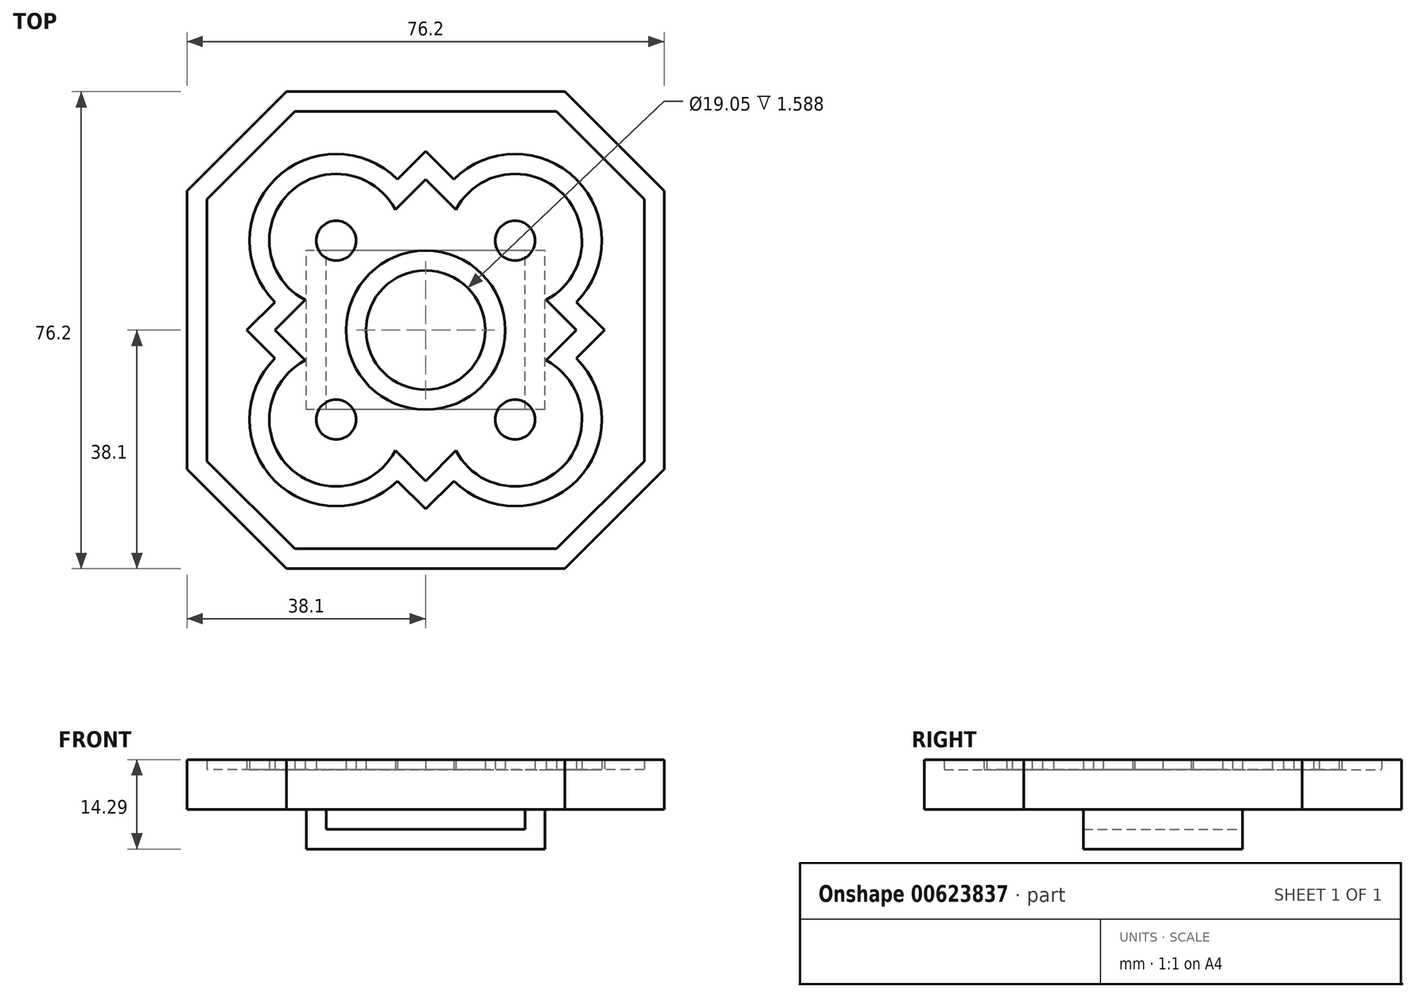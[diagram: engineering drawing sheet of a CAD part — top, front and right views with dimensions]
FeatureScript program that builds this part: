
annotation { "Feature Type Name" : "Feature", "Feature Type Description" : "" }
export const myFeature = defineFeature(function(context is Context, id is Id, definition is map)
    precondition{}
    {
        {
            var Q0;
            Q0=qCreatedBy(makeId("Top.planeOp"),FACE);
            var sketch = newSketch(context, id + "F0", { "sketchPlane" : qUnion([Q0])});
            skLineSegment(sketch, "E0.bottom", {"start": v(-76.2, 0) * mm, "end": v(0, 0) * mm, "construction": true});
            skLineSegment(sketch, "E0.top", {"start": v(-76.2, -76.2) * mm, "end": v(0, -76.2) * mm, "construction": true});
            skLineSegment(sketch, "E0.left", {"start": v(-76.2, 0) * mm, "end": v(-76.2, -76.2) * mm, "construction": true});
            skLineSegment(sketch, "E0.right", {"start": v(0, 0) * mm, "end": v(0, -76.2) * mm, "construction": true});
            skLineSegment(sketch, "E1", {"start": v(-60.32, 0) * mm, "end": v(-15.87, 0) * mm});
            skLineSegment(sketch, "E2", {"start": v(0, -15.87) * mm, "end": v(0, -60.32) * mm});
            skLineSegment(sketch, "E3", {"start": v(-76.2, -15.87) * mm, "end": v(-76.2, -60.32) * mm});
            skLineSegment(sketch, "E4", {"start": v(-60.32, -76.2) * mm, "end": v(-15.87, -76.2) * mm});
            skPoint(sketch, "E5", {"position": v(-38.1, 0) * mm});
            skPoint(sketch, "E6", {"position": v(-76.2, -38.1) * mm});
            skPoint(sketch, "E7", {"position": v(-38.1, -76.2) * mm});
            skPoint(sketch, "E8", {"position": v(0, -38.1) * mm});
            skLineSegment(sketch, "E9", {"start": v(-60.32, -76.2) * mm, "end": v(-76.2, -60.32) * mm});
            skLineSegment(sketch, "E10", {"start": v(0, -60.32) * mm, "end": v(-15.87, -76.2) * mm});
            skLineSegment(sketch, "E11", {"start": v(-76.2, -15.87) * mm, "end": v(-60.32, 0) * mm});
            skLineSegment(sketch, "E12", {"start": v(-15.87, 0) * mm, "end": v(0, -15.87) * mm});
            skLineSegment(sketch, "E13", {"start": v(-38.1, 0) * mm, "end": v(-38.1, -76.2) * mm, "construction": true});
            skPoint(sketch, "E14", {"position": v(-38.1, -38.1) * mm});
            skSolve(sketch);
        }
        {
            var Q0;
            Q0=qSketchRegion(id+"F0",true);
            extrude(context, id + "F1", {"entities" : qUnion([Q0]), "depth" : 6.35 * mm, "offsetDistance" : 25.4 * mm});
        }
        {
            var Q0;
            Q0=makeQuery(id+"F1.opExtrude","CAP_FACE",FACE,{"disambiguationData":[OSD([sQuery(id+"F0.wireOp",EDGE,"E1"),sQuery(id+"F0.wireOp",EDGE,"E2"),sQuery(id+"F0.wireOp",EDGE,"E3"),sQuery(id+"F0.wireOp",EDGE,"E4"),sQuery(id+"F0.wireOp",EDGE,"E9"),sQuery(id+"F0.wireOp",EDGE,"E10"),sQuery(id+"F0.wireOp",EDGE,"E11"),sQuery(id+"F0.wireOp",EDGE,"E12")])],"isStart":false});
            var sketch = newSketch(context, id + "F2", { "sketchPlane" : qUnion([Q0])});
            skLineSegment(sketch, "E15", {"start": v(0, -38.1) * mm, "end": v(-76.2, -38.1) * mm, "construction": true});
            skCircle(sketch, "E16", {"center": v(-38.1, -38.1) * mm, "radius": 12.7 * mm});
            skCircle(sketch, "E17", {"center": v(-38.1, -38.1) * mm, "radius": 9.53 * mm});
            skLineSegment(sketch, "E18", {"start": v(-15.87, 0) * mm, "end": v(-60.32, 0) * mm});
            skLineSegment(sketch, "E19", {"start": v(0, -60.32) * mm, "end": v(-15.88, -76.2) * mm});
            skLineSegment(sketch, "E20", {"start": v(0, -60.32) * mm, "end": v(0, -15.87) * mm});
            skLineSegment(sketch, "E21", {"start": v(0, -15.88) * mm, "end": v(-15.87, 0) * mm});
            skLineSegment(sketch, "E22", {"start": v(-76.2, -15.87) * mm, "end": v(-60.32, 0) * mm});
            skLineSegment(sketch, "E23", {"start": v(-76.2, -60.32) * mm, "end": v(-60.33, -76.2) * mm});
            skLineSegment(sketch, "E24", {"start": v(-76.2, -15.87) * mm, "end": v(-76.2, -60.32) * mm});
            skLineSegment(sketch, "E25", {"start": v(-15.87, -76.2) * mm, "end": v(-60.32, -76.2) * mm});
            skLineSegment(sketch, "E26", {"start": v(-3.18, -59) * mm, "end": v(-3.18, -17.2) * mm});
            skLineSegment(sketch, "E27", {"start": v(-73.03, -59) * mm, "end": v(-73.03, -17.2) * mm});
            skLineSegment(sketch, "E28", {"start": v(-59, -73.02) * mm, "end": v(-17.2, -73.02) * mm});
            skLineSegment(sketch, "E29", {"start": v(-59, -3.17) * mm, "end": v(-17.2, -3.17) * mm});
            skLineSegment(sketch, "E30", {"start": v(-3.17, -17.2) * mm, "end": v(-17.2, -3.18) * mm});
            skLineSegment(sketch, "E31", {"start": v(-59, -73.02) * mm, "end": v(-73.02, -59) * mm});
            skLineSegment(sketch, "E32", {"start": v(-17.2, -73.02) * mm, "end": v(-3.18, -59) * mm});
            skLineSegment(sketch, "E33", {"start": v(-73.03, -17.2) * mm, "end": v(-59, -3.18) * mm});
            skLineSegment(sketch, "E34", {"start": v(-38.1, -73.02) * mm, "end": v(-38.1, -3.18) * mm, "construction": true});
            skLineSegment(sketch, "E35", {"start": v(-7.94, -7.94) * mm, "end": v(-68.26, -68.26) * mm, "construction": true});
            skLineSegment(sketch, "E36", {"start": v(-68.26, -7.94) * mm, "end": v(-7.94, -68.26) * mm, "construction": true});
            skLineSegment(sketch, "E37", {"start": v(-9.53, -38.1) * mm, "end": v(-38.1, -9.53) * mm, "construction": true});
            skLineSegment(sketch, "E38", {"start": v(-9.53, -38.1) * mm, "end": v(-38.1, -66.67) * mm, "construction": true});
            skLineSegment(sketch, "E39", {"start": v(-38.1, -66.67) * mm, "end": v(-66.67, -38.1) * mm, "construction": true});
            skLineSegment(sketch, "E40", {"start": v(-38.1, -9.53) * mm, "end": v(-66.67, -38.1) * mm, "construction": true});
            skCircle(sketch, "E41", {"center": v(-23.81, -52.39) * mm, "radius": 3.18 * mm});
            skCircle(sketch, "E42", {"center": v(-52.39, -52.39) * mm, "radius": 3.18 * mm});
            skCircle(sketch, "E43", {"center": v(-23.81, -23.81) * mm, "radius": 3.18 * mm});
            skCircle(sketch, "E44", {"center": v(-52.39, -23.81) * mm, "radius": 3.18 * mm});
            skLineSegment(sketch, "E45", {"start": v(-62.18, -38.1) * mm, "end": v(-38.1, -62.18) * mm, "construction": true});
            skLineSegment(sketch, "E46", {"start": v(-62.18, -38.1) * mm, "end": v(-38.1, -14.02) * mm, "construction": true});
            skLineSegment(sketch, "E47", {"start": v(-38.1, -14.02) * mm, "end": v(-14.02, -38.1) * mm, "construction": true});
            skLineSegment(sketch, "E48", {"start": v(-14.02, -38.1) * mm, "end": v(-38.1, -62.18) * mm, "construction": true});
            skArc(sketch, "E49", {"start": v(-33.6, -62.18) * mm, "mid": v(-14.02, -62.18) * mm, "end": v(-14.02, -42.6) * mm});
            skLineSegment(sketch, "E50", {"start": v(-14.02, -42.6) * mm, "end": v(-33.6, -62.18) * mm, "construction": true});
            skArc(sketch, "E51", {"start": v(-62.18, -42.6) * mm, "mid": v(-62.18, -62.18) * mm, "end": v(-42.6, -62.18) * mm});
            skArc(sketch, "E52", {"start": v(-42.6, -14.02) * mm, "mid": v(-62.18, -14.02) * mm, "end": v(-62.18, -33.6) * mm});
            skArc(sketch, "E53", {"start": v(-14.02, -33.6) * mm, "mid": v(-14.02, -14.02) * mm, "end": v(-33.6, -14.02) * mm});
            skLineSegment(sketch, "E54", {"start": v(-33.6, -62.18) * mm, "end": v(-38.1, -66.67) * mm});
            skLineSegment(sketch, "E55", {"start": v(-38.1, -66.67) * mm, "end": v(-42.6, -62.18) * mm});
            skLineSegment(sketch, "E56", {"start": v(-62.18, -42.6) * mm, "end": v(-66.67, -38.1) * mm});
            skLineSegment(sketch, "E57", {"start": v(-66.67, -38.1) * mm, "end": v(-62.18, -33.6) * mm});
            skLineSegment(sketch, "E58", {"start": v(-42.6, -14.02) * mm, "end": v(-38.1, -9.53) * mm});
            skLineSegment(sketch, "E59", {"start": v(-33.6, -14.02) * mm, "end": v(-38.1, -9.53) * mm});
            skLineSegment(sketch, "E60", {"start": v(-14.02, -33.6) * mm, "end": v(-9.53, -38.1) * mm});
            skLineSegment(sketch, "E61", {"start": v(-14.02, -42.6) * mm, "end": v(-9.53, -38.1) * mm});
            skArc(sketch, "E62", {"start": v(-18.85, -33.27) * mm, "mid": v(-16.26, -16.26) * mm, "end": v(-33.27, -18.85) * mm});
            skArc(sketch, "E63", {"start": v(-33.27, -57.35) * mm, "mid": v(-16.26, -59.94) * mm, "end": v(-18.85, -42.93) * mm});
            skArc(sketch, "E64", {"start": v(-57.35, -42.93) * mm, "mid": v(-59.94, -59.94) * mm, "end": v(-42.93, -57.35) * mm});
            skArc(sketch, "E65", {"start": v(-42.93, -18.85) * mm, "mid": v(-59.94, -16.26) * mm, "end": v(-57.35, -33.27) * mm});
            skLineSegment(sketch, "E66", {"start": v(-42.93, -57.35) * mm, "end": v(-38.1, -62.18) * mm});
            skLineSegment(sketch, "E67", {"start": v(-38.1, -62.18) * mm, "end": v(-33.27, -57.35) * mm});
            skLineSegment(sketch, "E68", {"start": v(-18.85, -42.93) * mm, "end": v(-14.02, -38.1) * mm});
            skLineSegment(sketch, "E69", {"start": v(-14.02, -38.1) * mm, "end": v(-18.85, -33.27) * mm});
            skLineSegment(sketch, "E70", {"start": v(-33.27, -18.85) * mm, "end": v(-38.1, -14.02) * mm});
            skLineSegment(sketch, "E71", {"start": v(-42.93, -18.85) * mm, "end": v(-38.1, -14.02) * mm});
            skLineSegment(sketch, "E72", {"start": v(-57.35, -33.27) * mm, "end": v(-62.18, -38.1) * mm});
            skLineSegment(sketch, "E73", {"start": v(-57.35, -42.93) * mm, "end": v(-62.18, -38.1) * mm});
            skSolve(sketch);
        }
        {
            var Q0;
            Q0=qSketchRegion(id+"F2",true);
            var Q1;
            Q1=makeQuery(id+"F2.imprint","IMPRINT",FACE,{"disambiguationData":[TD([[makeQuery(id+"F2.imprint","IMPRINT",EDGE,{"derivedFrom":sQuery(id+"F2.wireOp",EDGE,"E49")}),1.0]])]});
            var Q2;
            Q2=makeQuery(id+"F2.imprint","IMPRINT",FACE,{"disambiguationData":[TD([[makeQuery(id+"F2.imprint","IMPRINT",EDGE,{"derivedFrom":sQuery(id+"F2.wireOp",EDGE,"E16")}),1.0]])]});
            var Q3;
            Q3=makeQuery(id+"F2.imprint","IMPRINT",FACE,{"disambiguationData":[TD([[makeQuery(id+"F2.imprint","IMPRINT",EDGE,{"derivedFrom":sQuery(id+"F2.wireOp",EDGE,"E42")}),1.0]])]});
            var Q4;
            Q4=makeQuery(id+"F2.imprint","IMPRINT",FACE,{"disambiguationData":[TD([[makeQuery(id+"F2.imprint","IMPRINT",EDGE,{"derivedFrom":sQuery(id+"F2.wireOp",EDGE,"E41")}),1.0]])]});
            var Q5;
            Q5=makeQuery(id+"F2.imprint","IMPRINT",FACE,{"disambiguationData":[TD([[makeQuery(id+"F2.imprint","IMPRINT",EDGE,{"derivedFrom":sQuery(id+"F2.wireOp",EDGE,"E43")}),1.0]])]});
            var Q6;
            Q6=makeQuery(id+"F2.imprint","IMPRINT",FACE,{"disambiguationData":[TD([[makeQuery(id+"F2.imprint","IMPRINT",EDGE,{"derivedFrom":sQuery(id+"F2.wireOp",EDGE,"E44")}),1.0]])]});
            extrude(context, id + "F3", {"entities" : qUnion([Q0, Q1, Q2, Q3, Q4, Q5, Q6]), "operationType" : NewBodyOperationType.ADD, "depth" : 1.59 * mm, "offsetDistance" : 25.4 * mm});
        }
        {
            var Q0;
            Q0=makeQuery(id+"F1.opExtrude","CAP_FACE",FACE,{"disambiguationData":[OSD([sQuery(id+"F0.wireOp",EDGE,"E1"),sQuery(id+"F0.wireOp",EDGE,"E2"),sQuery(id+"F0.wireOp",EDGE,"E3"),sQuery(id+"F0.wireOp",EDGE,"E4"),sQuery(id+"F0.wireOp",EDGE,"E9"),sQuery(id+"F0.wireOp",EDGE,"E10"),sQuery(id+"F0.wireOp",EDGE,"E11"),sQuery(id+"F0.wireOp",EDGE,"E12")])],"isStart":true});
            var sketch = newSketch(context, id + "F4", { "sketchPlane" : qUnion([Q0])});
            skLineSegment(sketch, "E74", {"start": v(0, 38.1) * mm, "end": v(-76.2, 38.1) * mm, "construction": true});
            skLineSegment(sketch, "E75.bottom", {"start": v(-53.97, 50.8) * mm, "end": v(-57.15, 50.8) * mm});
            skLineSegment(sketch, "E75.top", {"start": v(-53.97, 25.4) * mm, "end": v(-57.15, 25.4) * mm});
            skLineSegment(sketch, "E75.left", {"start": v(-53.97, 50.8) * mm, "end": v(-53.97, 25.4) * mm});
            skLineSegment(sketch, "E75.right", {"start": v(-57.15, 50.8) * mm, "end": v(-57.15, 25.4) * mm});
            skLineSegment(sketch, "E76.bottom", {"start": v(-19.05, 50.8) * mm, "end": v(-22.22, 50.8) * mm});
            skLineSegment(sketch, "E76.top", {"start": v(-19.05, 25.4) * mm, "end": v(-22.22, 25.4) * mm});
            skLineSegment(sketch, "E76.left", {"start": v(-19.05, 50.8) * mm, "end": v(-19.05, 25.4) * mm});
            skLineSegment(sketch, "E76.right", {"start": v(-22.22, 50.8) * mm, "end": v(-22.22, 25.4) * mm});
            skLineSegment(sketch, "E77", {"start": v(-19.05, 38.1) * mm, "end": v(-57.15, 38.1) * mm, "construction": true});
            skPoint(sketch, "E78", {"position": v(-38.1, 38.1) * mm});
            skSolve(sketch);
        }
        {
            var Q0;
            Q0=qSketchRegion(id+"F4",true);
            extrude(context, id + "F5", {"entities" : qUnion([Q0]), "operationType" : NewBodyOperationType.ADD, "depth" : 3.17 * mm, "offsetDistance" : 25.4 * mm});
        }
        {
            var Q0;
            Q0=makeQuery(id+"F5.opExtrude","CAP_FACE",FACE,{"disambiguationData":[OSD([sQuery(id+"F4.wireOp",EDGE,"E76.bottom"),sQuery(id+"F4.wireOp",EDGE,"E76.top"),sQuery(id+"F4.wireOp",EDGE,"E76.left"),sQuery(id+"F4.wireOp",EDGE,"E76.right")])],"isStart":false});
            var sketch = newSketch(context, id + "F6", { "sketchPlane" : qUnion([Q0])});
            skLineSegment(sketch, "E79.bottom", {"start": v(-19.05, 50.8) * mm, "end": v(-57.15, 50.8) * mm});
            skLineSegment(sketch, "E79.top", {"start": v(-19.05, 25.4) * mm, "end": v(-57.15, 25.4) * mm});
            skLineSegment(sketch, "E79.left", {"start": v(-19.05, 50.8) * mm, "end": v(-19.05, 25.4) * mm});
            skLineSegment(sketch, "E79.right", {"start": v(-57.15, 50.8) * mm, "end": v(-57.15, 25.4) * mm});
            skSolve(sketch);
        }
        {
            var Q0;
            Q0=qSketchRegion(id+"F6",true);
            extrude(context, id + "F7", {"entities" : qUnion([Q0]), "operationType" : NewBodyOperationType.ADD, "depth" : 3.17 * mm, "offsetDistance" : 25.4 * mm});
        }
    });
